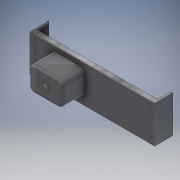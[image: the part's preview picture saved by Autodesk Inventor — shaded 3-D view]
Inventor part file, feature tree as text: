
AUTODESK INVENTOR PART (.ipt)
format: ipt  version: 2017 (Build 210142000, 142)  size: 985,600 bytes
history: native  units: mm
features: sheet_metal_op x40, sketch x27, other x22, extrude x9, reference x4, plane x1, hole x1, projected_geometry x1
ambient origin geometry x8: Origin, YZ Plane, XZ Plane, XY Plane, X Axis, Y Axis, Z Axis, Center Point
bodies: Solid1 (feature_tree)
feature tree (105):
  sheet_metal_op  "Face1"
  sheet_metal_op  "Flange3"
  sheet_metal_op  "Flange4"
  sheet_metal_op  "Flange5"
  extrude  "Extrusion1"  Depth=260.0mm
  sheet_metal_op  "Flange10"
  sheet_metal_op  "Flange11"
  sheet_metal_op  "Flange12"
  extrude  "Extrusion6"  Depth=1.5mm
  sheet_metal_op  "Flange13"
  sheet_metal_op  "Flange14"
  sheet_metal_op  "Flange15"
  sheet_metal_op  "Flange16"
  sheet_metal_op  "Flange17"
  plane  "Work Plane2"
  other  "Decal2"
  extrude  "Extrusion7"  Depth=1.5mm
  sheet_metal_op  "Flange18"
  sheet_metal_op  "Flange19"
  extrude  "Extrusion8"  Depth=1.5mm
  extrude  "Extrusion15"  Depth=1.5mm
  extrude  "Extrusion16"  Depth=1.5mm
  extrude  "Extrusion17"  Depth=1.5mm
  extrude  "Extrusion18"  Depth=1.5mm
  extrude  "Extrusion19"  Depth=1.5mm
  hole  "Hole1"  [1 undecoded]
  sketch  "Sketch1"  dims[d0=900.0mm d1=260.0mm]
  other  "Plate1"
  sketch  "Sketch3"  dims[d2=1.5mm d12=15.0mm d13=1.5mm]
  sketch  "Sketch7"  dims[d39=1.5mm d41=1.5mm]
  other  "Plate4"
  sheet_metal_op  "Bend3"
  sheet_metal_op  "Corner3"
  sketch  "Sketch8"  dims[d43=1.5mm d44=0.75mm]
  other  "Plate5"
  sheet_metal_op  "Bend4"
  sheet_metal_op  "Corner4"
  sketch  "Sketch9"  dims[d45=3.0mm d46=1.5mm]
  other  "Plate6"
  sheet_metal_op  "Bend5"
  sheet_metal_op  "Corner5"
  sketch  "Sketch10"  dims[d47=86.0mm d48=90.0deg d49=1.5mm d50=6.0mm]
  sketch  "Sketch21"  dims[d51=1.5mm d52=1.5mm]
  other  "Plate11"
  sheet_metal_op  "Bend10"
  sheet_metal_op  "Corner10"
  sketch  "Sketch22"  dims[d53=1.5mm d54=0.75mm]
  other  "Plate12"
  sheet_metal_op  "Bend11"
  sheet_metal_op  "Corner11"
  sketch  "Sketch23"  dims[d55=3.0mm d56=1.5mm]
  other  "Plate13"
  sheet_metal_op  "Bend12"
  sheet_metal_op  "Corner12"
  sketch  "Sketch24"  dims[d57=28.0mm d58=45.0deg d59=1.5mm d60=6.0mm]
  sketch  "Sketch25"  dims[d61=1.5mm]
  other  "Plate14"
  sheet_metal_op  "Bend13"
  sheet_metal_op  "Corner13"
  sketch  "Sketch26"  dims[d62=1.5mm]
  other  "Plate15"
  sheet_metal_op  "Bend14"
  sheet_metal_op  "Corner14"
  sketch  "Sketch27"  dims[d63=1.5mm]
  other  "Plate16"
  sheet_metal_op  "Bend15"
  sheet_metal_op  "Corner15"
  sketch  "Sketch28"  dims[d64=0.75mm]
  other  "Plate17"
  sheet_metal_op  "Bend16"
  sheet_metal_op  "Corner16"
  sketch  "Sketch29"  dims[d65=3.0mm]
  other  "Plate18"
  sheet_metal_op  "Bend17"
  sheet_metal_op  "Corner17"
  sketch  "Sketch30"  dims[d66=1.5mm]
  other  "Image2"
  sketch  "Sketch31"  dims[d67=16.0mm d68=135.0deg d69=1.5mm]
  sketch  "Sketch32"  dims[d70=6.0mm]
  other  "Plate19"
  sheet_metal_op  "Bend18"
  sheet_metal_op  "Corner18"
  sketch  "Sketch33"  dims[d71=1.5mm]
  other  "Plate20"
  sheet_metal_op  "Bend19"
  sheet_metal_op  "Corner19"
  sketch  "Sketch34"  dims[d72=1.5mm]
  projected_geometry  "Projected Loop7"
  sketch  "Sketch35"  dims[d74=130.0mm]
  sketch  "Sketch42"  dims[d75=19.05mm]
  sketch  "Sketch43"  dims[d76=1.5mm]
  sketch  "Sketch44"  dims[d77=0.0mm]
  sketch  "Sketch45"  dims[d145=0.0mm]
  sketch  "Sketch46"  dims[d147=270.0mm]
  sketch  "Sketch47"  dims[d148=20.0mm d149=20.0mm d150=0.0mm d151=1.5mm d152=0.75mm d153=3.0mm d154=1.5mm d155=40.0mm d156=90.0deg d157=1.5mm d158=6.0mm d159=1.5mm d160=1.5mm d161=1.5mm d162=0.75mm d163=3.0mm d164=1.5mm d165=10.0mm d166=90.0deg d167=1.5mm d168=6.0mm d169=1.5mm d170=1.5mm d171=1.5mm d172=0.75mm d173=3.0mm d174=1.5mm d175=19.799mm d176=90.0deg d177=1.5mm d178=6.0mm d179=1.5mm d180=1.5mm d181=1.5mm d182=0.0mm d183=1.5mm d184=0.75mm d185=3.0mm d186=1.5mm d187=19.799mm d188=0.0mm d189=1.5mm d190=6.0mm d191=1.5mm d192=1.5mm d193=1.5mm d194=0.75mm d195=3.0mm d196=1.5mm d197=41.5mm d198=0.0mm d199=1.5mm d200=6.0mm d201=1.5mm d202=1.5mm d203=1.5mm d204=0.75mm d205=3.0mm d206=1.5mm d207=10.0mm d208=90.0deg d209=1.5mm d210=6.0mm d211=1.5mm d212=1.5mm d213=1.5mm d214=0.75mm d215=3.0mm d216=1.5mm d217=4.5mm d218=0.0mm d219=1.5mm d220=6.0mm d221=1.5mm d222=1.5mm d223=1.5mm d224=0.75mm d225=3.0mm d226=1.5mm d227=4.5mm d228=0.0mm d229=1.5mm d230=6.0mm d231=1.5mm d232=1.5mm d233=400.0mm d239=1.5mm d240=0.0mm d241=1.5mm d242=0.75mm d243=3.0mm d244=1.5mm d245=0.0mm d246=10.0mm d247=10.0mm d248=90.0deg d249=1.5mm d250=6.0mm d251=1.5mm d252=1.5mm d253=1.5mm d254=0.75mm d255=3.0mm d256=1.5mm d257=8.0mm d258=0.0mm d259=10.0mm d260=90.0deg d261=1.5mm d262=6.0mm d263=1.5mm d264=1.5mm d266=15.0mm d267=1.5mm d269=1.5mm d270=1.5mm d272=1.5mm d273=0.0mm d274=0.0mm d287=10.0mm d288=0.0mm d289=10.0mm d290=0.0mm d291=10.0mm d292=0.0mm d293=10.0mm d294=0.0mm d295=40.0mm d296=268.0mm d297=40.0mm d298=268.0mm d299=1.5mm d300=0.0mm d301=6.647mm d302=16.0mm d303=4.0mm d304=2.0mm d305=90.0deg d306=22.2mm d307=20.594885mm]
  reference  "Reference1"
  reference  "Reference2"
  reference  "Reference3"
  reference  "Reference4"
  other  "iFeature1:1"
  other  "iFeature5:1"
  other  "iFeature1:3"
  other  "Bancada de Lavagem Mãos - 1150 x 370 x 900h.iam"
  other  "Lateral -A1:1"
  other  "Lateral -A:1"
note: 1 required parameter value undecoded (feature->parameter linkage not recoverable at this tier; creation-order binding heuristic only, values carry confidence <= 0.55)
